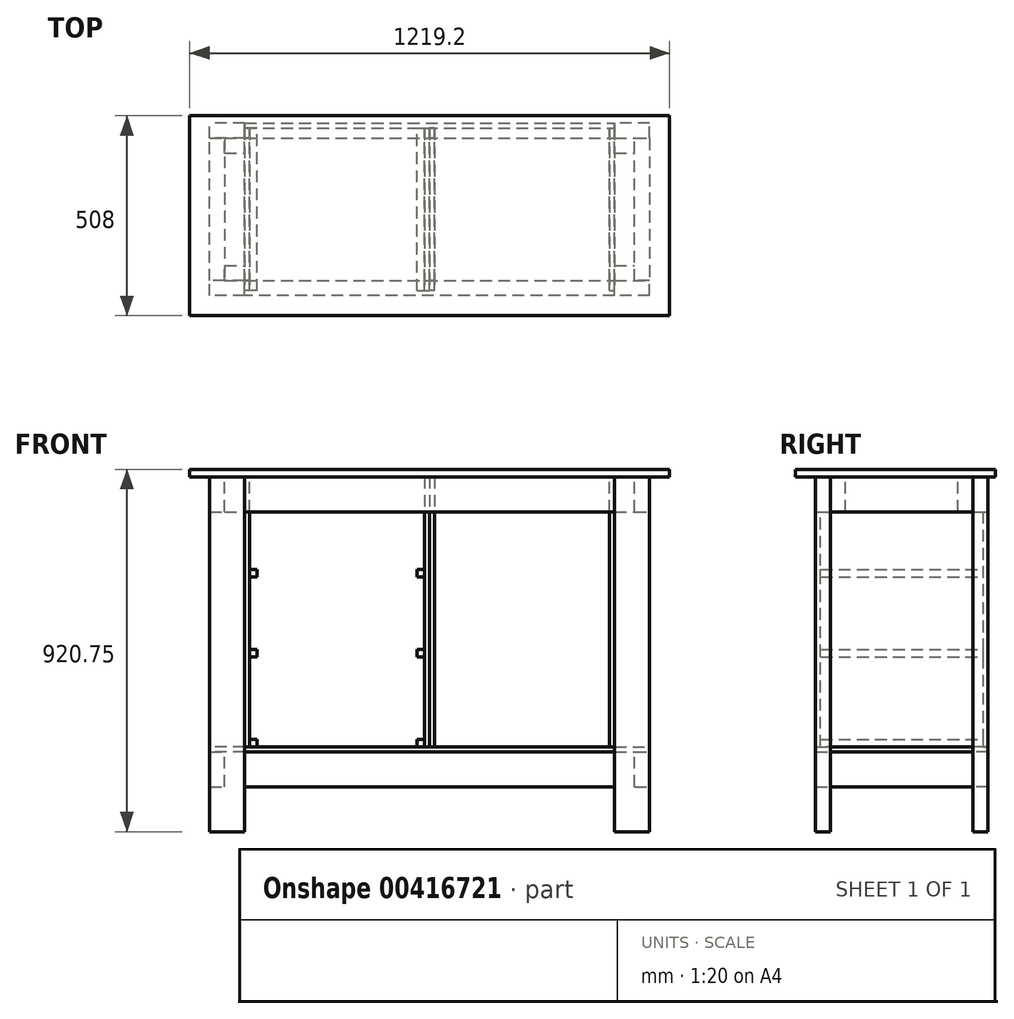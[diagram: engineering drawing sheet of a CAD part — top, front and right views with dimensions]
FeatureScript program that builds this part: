
annotation { "Feature Type Name" : "Feature", "Feature Type Description" : "" }
export const myFeature = defineFeature(function(context is Context, id is Id, definition is map)
    precondition{}
    {
        {
            var Q0;
            Q0=qCreatedBy(makeId("Front.planeOp"),FACE);
            var sketch = newSketch(context, id + "F0", { "sketchPlane" : qUnion([Q0])});
            skLineSegment(sketch, "E0.bottom", {"start": v(-609.6, 19.05) * mm, "end": v(609.6, 19.05) * mm});
            skLineSegment(sketch, "E0.top", {"start": v(-609.6, 0) * mm, "end": v(609.6, 0) * mm});
            skLineSegment(sketch, "E0.left", {"start": v(-609.6, 19.05) * mm, "end": v(-609.6, 0) * mm});
            skLineSegment(sketch, "E0.right", {"start": v(609.6, 19.05) * mm, "end": v(609.6, 0) * mm});
            skSolve(sketch);
        }
        {
            var Q0;
            Q0=qSketchRegion(id+"F0",true);
            extrude(context, id + "F1", {"entities" : qUnion([Q0]), "oppositeDirection" : true, "depth" : 508 * mm, "offsetDistance" : 25.4 * mm});
        }
        {
            var Q0;
            Q0=makeQuery(id+"F1.opExtrude","SWEPT_FACE",FACE,{"disambiguationData":[OSD([sQuery(id+"F0.wireOp",EDGE,"E0.top")])]});
            var sketch = newSketch(context, id + "F2", { "sketchPlane" : qUnion([Q0])});
            skLineSegment(sketch, "E1.0", {"start": v(558.8, -50.8) * mm, "end": v(-558.8, -50.8) * mm, "construction": true});
            skLineSegment(sketch, "E1.1", {"start": v(558.8, -488.95) * mm, "end": v(558.8, -50.8) * mm, "construction": true});
            skLineSegment(sketch, "E1.2", {"start": v(-558.8, -488.95) * mm, "end": v(558.8, -488.95) * mm, "construction": true});
            skLineSegment(sketch, "E1.3", {"start": v(-558.8, -50.8) * mm, "end": v(-558.8, -488.95) * mm, "construction": true});
            skSolve(sketch);
        }
        {
            var Q0;
            {var subQ0=sQuery(id+"F0.wireOp",EDGE,"E0.top");Q0=makeQuery(id+"F2.imprint","IMPRINT",FACE,{"disambiguationData":[TD([[makeQuery(id+"F2.imprint","IMPRINT",EDGE,{"derivedFrom":makeQuery(id+"F1.opExtrude","CAP_EDGE",EDGE,{"disambiguationData":[OSD([subQ0])],"isStart":true})}),-1.0]])]});}
            var sketch = newSketch(context, id + "F3", { "sketchPlane" : qUnion([Q0])});
            skLineSegment(sketch, "E2.bottom", {"start": v(558.8, -50.8) * mm, "end": v(469.9, -50.8) * mm});
            skLineSegment(sketch, "E2.top", {"start": v(558.8, -88.9) * mm, "end": v(469.9, -88.9) * mm});
            skLineSegment(sketch, "E2.left", {"start": v(558.8, -50.8) * mm, "end": v(558.8, -88.9) * mm});
            skLineSegment(sketch, "E2.right", {"start": v(469.9, -50.8) * mm, "end": v(469.9, -88.9) * mm});
            skLineSegment(sketch, "E3.bottom", {"start": v(-469.9, -50.8) * mm, "end": v(-558.8, -50.8) * mm});
            skLineSegment(sketch, "E3.top", {"start": v(-469.9, -88.9) * mm, "end": v(-558.8, -88.9) * mm});
            skLineSegment(sketch, "E3.left", {"start": v(-469.9, -50.8) * mm, "end": v(-469.9, -88.9) * mm});
            skLineSegment(sketch, "E3.right", {"start": v(-558.8, -50.8) * mm, "end": v(-558.8, -88.9) * mm});
            skLineSegment(sketch, "E4.bottom", {"start": v(-469.9, -450.85) * mm, "end": v(-558.8, -450.85) * mm});
            skLineSegment(sketch, "E4.top", {"start": v(-469.9, -488.95) * mm, "end": v(-558.8, -488.95) * mm});
            skLineSegment(sketch, "E4.left", {"start": v(-469.9, -450.85) * mm, "end": v(-469.9, -488.95) * mm});
            skLineSegment(sketch, "E4.right", {"start": v(-558.8, -450.85) * mm, "end": v(-558.8, -488.95) * mm});
            skLineSegment(sketch, "E5.bottom", {"start": v(558.8, -450.85) * mm, "end": v(469.9, -450.85) * mm});
            skLineSegment(sketch, "E5.top", {"start": v(558.8, -488.95) * mm, "end": v(469.9, -488.95) * mm});
            skLineSegment(sketch, "E5.left", {"start": v(558.8, -450.85) * mm, "end": v(558.8, -488.95) * mm});
            skLineSegment(sketch, "E5.right", {"start": v(469.9, -450.85) * mm, "end": v(469.9, -488.95) * mm});
            skSolve(sketch);
        }
        {
            var Q0;
            Q0=qSketchRegion(id+"F3",true);
            extrude(context, id + "F4", {"entities" : qUnion([Q0]), "depth" : 901.7 * mm, "offsetDistance" : 25.4 * mm});
        }
        {
            var Q0;
            {var subQ0=sQuery(id+"F0.wireOp",EDGE,"E0.top");Q0=makeQuery(id+"F2.imprint","IMPRINT",FACE,{"disambiguationData":[TD([[makeQuery(id+"F2.imprint","IMPRINT",EDGE,{"derivedFrom":makeQuery(id+"F1.opExtrude","CAP_EDGE",EDGE,{"disambiguationData":[OSD([subQ0])],"isStart":true})}),-1.0]])]});}
            var sketch = newSketch(context, id + "F5", { "sketchPlane" : qUnion([Q0])});
            skLineSegment(sketch, "E6.left", {"start": v(-558.8, -50.8) * mm, "end": v(-558.8, -50.8) * mm});
            skLineSegment(sketch, "E6.right", {"start": v(558.8, -50.8) * mm, "end": v(558.8, -50.8) * mm});
            skLineSegment(sketch, "E7.left", {"start": v(-558.8, -488.95) * mm, "end": v(-558.8, -488.95) * mm});
            skLineSegment(sketch, "E7.right", {"start": v(558.8, -488.95) * mm, "end": v(558.8, -488.95) * mm});
            skLineSegment(sketch, "E8.bottom", {"start": v(-469.9, -50.8) * mm, "end": v(469.9, -50.8) * mm});
            skLineSegment(sketch, "E8.top", {"start": v(-469.9, -88.9) * mm, "end": v(469.9, -88.9) * mm});
            skLineSegment(sketch, "E8.left", {"start": v(-469.9, -50.8) * mm, "end": v(-469.9, -88.9) * mm});
            skLineSegment(sketch, "E8.right", {"start": v(469.9, -50.8) * mm, "end": v(469.9, -88.9) * mm});
            skSolve(sketch);
        }
        {
            var Q0;
            Q0=makeQuery(id+"F5.imprint","IMPRINT",FACE,{"disambiguationData":[TD([[makeQuery(id+"F5.imprint","IMPRINT",EDGE,{"derivedFrom":sQuery(id+"F5.wireOp",EDGE,"E8.bottom")}),1.0]])]});
            var sketch = newSketch(context, id + "F6", { "sketchPlane" : qUnion([Q0])});
            skLineSegment(sketch, "E9.bottom", {"start": v(-469.9, -450.85) * mm, "end": v(469.9, -450.85) * mm});
            skLineSegment(sketch, "E9.top", {"start": v(-469.9, -488.95) * mm, "end": v(469.9, -488.95) * mm});
            skLineSegment(sketch, "E9.left", {"start": v(-469.9, -450.85) * mm, "end": v(-469.9, -488.95) * mm});
            skLineSegment(sketch, "E9.right", {"start": v(469.9, -450.85) * mm, "end": v(469.9, -488.95) * mm});
            skSolve(sketch);
        }
        {
            var Q0;
            Q0 = qSketchRegion(id + "F6", true);
            extrude(context, id + "F7", {"entities" : qUnion([Q0]), "depth" : 88.9 * mm, "offsetDistance" : 25.4 * mm});
        }
        {
            var Q0;
            Q0=qSketchRegion(id+"F5",true);
            extrude(context, id + "F8", {"entities" : qUnion([Q0]), "depth" : 88.9 * mm, "offsetDistance" : 25.4 * mm});
        }
        {
            var Q0;
            {var subQ0=sQuery(id+"F0.wireOp",EDGE,"E0.top");Q0=makeQuery(id+"F2.imprint","IMPRINT",FACE,{"disambiguationData":[TD([[makeQuery(id+"F2.imprint","IMPRINT",EDGE,{"derivedFrom":makeQuery(id+"F1.opExtrude","CAP_EDGE",EDGE,{"disambiguationData":[OSD([subQ0])],"isStart":true})}),-1.0]])]});}
            var sketch = newSketch(context, id + "F9", { "sketchPlane" : qUnion([Q0])});
            skLineSegment(sketch, "E10.bottom", {"start": v(-558.8, -88.9) * mm, "end": v(-520.7, -88.9) * mm});
            skLineSegment(sketch, "E10.top", {"start": v(-558.8, -450.85) * mm, "end": v(-520.7, -450.85) * mm});
            skLineSegment(sketch, "E10.left", {"start": v(-520.7, -88.9) * mm, "end": v(-520.7, -450.85) * mm});
            skLineSegment(sketch, "E10.right", {"start": v(-558.8, -88.9) * mm, "end": v(-558.8, -450.85) * mm});
            skLineSegment(sketch, "E11.bottom", {"start": v(520.7, -88.9) * mm, "end": v(558.8, -88.9) * mm});
            skLineSegment(sketch, "E11.top", {"start": v(520.7, -450.85) * mm, "end": v(558.8, -450.85) * mm});
            skLineSegment(sketch, "E11.left", {"start": v(558.8, -88.9) * mm, "end": v(558.8, -450.85) * mm});
            skLineSegment(sketch, "E11.right", {"start": v(520.7, -88.9) * mm, "end": v(520.7, -450.85) * mm});
            skSolve(sketch);
        }
        {
            var Q0;
            Q0=qSketchRegion(id+"F9",true);
            extrude(context, id + "F10", {"entities" : qUnion([Q0]), "depth" : 88.9 * mm, "offsetDistance" : 25.4 * mm});
        }
        {
            var Q0;
            Q0=makeQuery(id+"F1.opExtrude","SWEPT_FACE",FACE,{"disambiguationData":[OSD([sQuery(id+"F0.wireOp",EDGE,"E0.top")])]});
            var sketch = newSketch(context, id + "F11", { "sketchPlane" : qUnion([Q0])});
            skLineSegment(sketch, "E12.bottom", {"start": v(-520.7, -88.9) * mm, "end": v(-469.9, -88.9) * mm});
            skLineSegment(sketch, "E12.top", {"start": v(-520.7, -127) * mm, "end": v(-469.9, -127) * mm});
            skLineSegment(sketch, "E12.left", {"start": v(-520.7, -88.9) * mm, "end": v(-520.7, -127) * mm});
            skLineSegment(sketch, "E12.right", {"start": v(-469.9, -88.9) * mm, "end": v(-469.9, -127) * mm});
            skLineSegment(sketch, "E13.bottom", {"start": v(-520.7, -412.75) * mm, "end": v(-469.9, -412.75) * mm});
            skLineSegment(sketch, "E13.top", {"start": v(-520.7, -450.85) * mm, "end": v(-469.9, -450.85) * mm});
            skLineSegment(sketch, "E13.left", {"start": v(-520.7, -412.75) * mm, "end": v(-520.7, -450.85) * mm});
            skLineSegment(sketch, "E13.right", {"start": v(-469.9, -412.75) * mm, "end": v(-469.9, -450.85) * mm});
            skLineSegment(sketch, "E14.bottom", {"start": v(469.9, -88.9) * mm, "end": v(520.7, -88.9) * mm});
            skLineSegment(sketch, "E14.top", {"start": v(469.9, -127) * mm, "end": v(520.7, -127) * mm});
            skLineSegment(sketch, "E14.left", {"start": v(469.9, -88.9) * mm, "end": v(469.9, -127) * mm});
            skLineSegment(sketch, "E14.right", {"start": v(520.7, -88.9) * mm, "end": v(520.7, -127) * mm});
            skLineSegment(sketch, "E15.bottom", {"start": v(469.9, -412.75) * mm, "end": v(520.7, -412.75) * mm});
            skLineSegment(sketch, "E15.top", {"start": v(469.9, -450.85) * mm, "end": v(520.7, -450.85) * mm});
            skLineSegment(sketch, "E15.left", {"start": v(469.9, -412.75) * mm, "end": v(469.9, -450.85) * mm});
            skLineSegment(sketch, "E15.right", {"start": v(520.7, -412.75) * mm, "end": v(520.7, -450.85) * mm});
            skSolve(sketch);
        }
        {
            var Q0;
            Q0 = qSketchRegion(id + "F11", true);
            extrude(context, id + "F12", {"entities" : qUnion([Q0]), "depth" : 88.9 * mm, "offsetDistance" : 25.4 * mm});
        }
        {
            var Q0;
            Q0=makeQuery(id+"F4.opExtrude","CAP_FACE",FACE,{"disambiguationData":[OSD([sQuery(id+"F3.wireOp",EDGE,"E3.bottom"),sQuery(id+"F3.wireOp",EDGE,"E3.top"),sQuery(id+"F3.wireOp",EDGE,"E3.left"),sQuery(id+"F3.wireOp",EDGE,"E3.right")])],"isStart":false});
            cPlane(context, id + "F13", {"entities" : qUnion([Q0]), "cplaneType" : CPlaneType.OFFSET, "offset" : 203.2 * mm, "oppositeDirection" : true, "width" : 152.4 * mm, "height" : 152.4 * mm});
        }
        {
            var Q0;
            Q0=qCreatedBy(id+"F13.planeOp",FACE);
            var sketch = newSketch(context, id + "F14", { "sketchPlane" : qUnion([Q0])});
            skLineSegment(sketch, "E16.0.0", {"start": v(-469.9, -50.8) * mm, "end": v(-469.9, -88.9) * mm});
            skLineSegment(sketch, "E16.0.1", {"start": v(-469.9, -88.9) * mm, "end": v(469.9, -88.9) * mm});
            skLineSegment(sketch, "E16.0.2", {"start": v(469.9, -88.9) * mm, "end": v(469.9, -50.8) * mm});
            skLineSegment(sketch, "E16.0.3", {"start": v(469.9, -50.8) * mm, "end": v(-469.9, -50.8) * mm});
            skLineSegment(sketch, "E17.0.0", {"start": v(-469.9, -488.95) * mm, "end": v(-469.9, -450.85) * mm});
            skLineSegment(sketch, "E17.0.1", {"start": v(-469.9, -450.85) * mm, "end": v(469.9, -450.85) * mm});
            skLineSegment(sketch, "E17.0.2", {"start": v(469.9, -488.95) * mm, "end": v(469.9, -450.85) * mm});
            skLineSegment(sketch, "E17.0.3", {"start": v(469.9, -488.95) * mm, "end": v(-469.9, -488.95) * mm});
            skSolve(sketch);
        }
        {
            var Q0;
            Q0=qSketchRegion(id+"F14",true);
            extrude(context, id + "F15", {"entities" : qUnion([Q0]), "depth" : 88.9 * mm, "offsetDistance" : 25.4 * mm});
        }
        {
            var Q0;
            Q0=qCreatedBy(id+"F13.planeOp",FACE);
            var sketch = newSketch(context, id + "F16", { "sketchPlane" : qUnion([Q0])});
            skLineSegment(sketch, "E18.0.0", {"start": v(-520.7, -450.85) * mm, "end": v(-520.7, -88.9) * mm});
            skLineSegment(sketch, "E18.0.1", {"start": v(-558.8, -450.85) * mm, "end": v(-520.7, -450.85) * mm});
            skLineSegment(sketch, "E18.0.2", {"start": v(-558.8, -88.9) * mm, "end": v(-558.8, -450.85) * mm});
            skLineSegment(sketch, "E18.0.3", {"start": v(-520.7, -88.9) * mm, "end": v(-558.8, -88.9) * mm});
            skLineSegment(sketch, "E19.0.0", {"start": v(558.8, -450.85) * mm, "end": v(558.8, -88.9) * mm});
            skLineSegment(sketch, "E19.0.1", {"start": v(520.7, -450.85) * mm, "end": v(558.8, -450.85) * mm});
            skLineSegment(sketch, "E19.0.2", {"start": v(520.7, -88.9) * mm, "end": v(520.7, -450.85) * mm});
            skLineSegment(sketch, "E19.0.3", {"start": v(558.8, -88.9) * mm, "end": v(520.7, -88.9) * mm});
            skSolve(sketch);
        }
        {
            var Q0;
            Q0=qSketchRegion(id+"F16",true);
            extrude(context, id + "F17", {"entities" : qUnion([Q0]), "depth" : 88.9 * mm, "offsetDistance" : 25.4 * mm});
        }
        {
            var Q0;
            Q0=qCreatedBy(id+"F13.planeOp",FACE);
            var sketch = newSketch(context, id + "F18", { "sketchPlane" : qUnion([Q0])});
            skLineSegment(sketch, "E20", {"start": v(558.8, -450.85) * mm, "end": v(558.8, -88.9) * mm});
            skLineSegment(sketch, "E21", {"start": v(469.9, -50.8) * mm, "end": v(-469.9, -50.8) * mm});
            skLineSegment(sketch, "E22", {"start": v(-558.8, -88.9) * mm, "end": v(-558.8, -450.85) * mm});
            skLineSegment(sketch, "E23", {"start": v(-469.9, -488.95) * mm, "end": v(469.9, -488.95) * mm});
            skLineSegment(sketch, "E24", {"start": v(-469.9, -50.8) * mm, "end": v(-469.9, -88.9) * mm});
            skLineSegment(sketch, "E25", {"start": v(-469.9, -88.9) * mm, "end": v(-558.8, -88.9) * mm});
            skLineSegment(sketch, "E26", {"start": v(-469.9, -488.95) * mm, "end": v(-469.9, -450.85) * mm});
            skLineSegment(sketch, "E27", {"start": v(-469.9, -450.85) * mm, "end": v(-558.8, -450.85) * mm});
            skLineSegment(sketch, "E28", {"start": v(469.9, -488.95) * mm, "end": v(469.9, -450.85) * mm});
            skLineSegment(sketch, "E29", {"start": v(469.9, -450.85) * mm, "end": v(558.8, -450.85) * mm});
            skLineSegment(sketch, "E30", {"start": v(469.9, -50.8) * mm, "end": v(469.9, -88.9) * mm});
            skLineSegment(sketch, "E31", {"start": v(469.9, -88.9) * mm, "end": v(558.8, -88.9) * mm});
            skSolve(sketch);
        }
        {
            var Q0;
            Q0=qSketchRegion(id+"F18",true);
            extrude(context, id + "F19", {"entities" : qUnion([Q0]), "oppositeDirection" : true, "depth" : 12.7 * mm, "offsetDistance" : 25.4 * mm});
        }
        {
            var Q0;
            Q0=qCreatedBy(makeId("Right.planeOp"),FACE);
            var sketch = newSketch(context, id + "F20", { "sketchPlane" : qUnion([Q0])});
            skLineSegment(sketch, "E32", {"start": v(450.85, 0) * mm, "end": v(450.85, -88.9) * mm});
            skLineSegment(sketch, "E33", {"start": v(450.85, -88.9) * mm, "end": v(476.25, -88.9) * mm});
            skLineSegment(sketch, "E34", {"start": v(476.25, -88.9) * mm, "end": v(476.25, -685.8) * mm});
            skLineSegment(sketch, "E35", {"start": v(476.25, -685.8) * mm, "end": v(63.5, -685.8) * mm});
            skLineSegment(sketch, "E36", {"start": v(63.5, -685.8) * mm, "end": v(63.5, -88.9) * mm});
            skLineSegment(sketch, "E37", {"start": v(63.5, -88.9) * mm, "end": v(88.9, -88.9) * mm});
            skLineSegment(sketch, "E38", {"start": v(88.9, -88.9) * mm, "end": v(88.9, 0) * mm});
            skLineSegment(sketch, "E39", {"start": v(88.9, 0) * mm, "end": v(450.85, 0) * mm});
            skSolve(sketch);
        }
        {
            var Q0;
            Q0 = qSketchRegion(id + "F20", true);
            extrude(context, id + "F21", {"entities" : qUnion([Q0]), "depth" : 12.7 * mm, "offsetDistance" : 25.4 * mm});
        }
        {
            var Q0;
            Q0 = qSketchRegion(id + "F20", true);
            extrude(context, id + "F22", {"entities" : qUnion([Q0]), "oppositeDirection" : true, "depth" : 12.7 * mm, "offsetDistance" : 25.4 * mm});
        }
        {
            var Q0;
            Q0=makeQuery(id+"F12.opExtrude","SWEPT_FACE",FACE,{"disambiguationData":[OSD([sQuery(id+"F11.wireOp",EDGE,"E13.right")])]});
            var sketch = newSketch(context, id + "F23", { "sketchPlane" : qUnion([Q0])});
            skLineSegment(sketch, "E40.0", {"start": v(450.85, 0) * mm, "end": v(450.85, -88.9) * mm});
            skLineSegment(sketch, "E40.1", {"start": v(450.85, -88.9) * mm, "end": v(476.25, -88.9) * mm});
            skLineSegment(sketch, "E40.2", {"start": v(476.25, -88.9) * mm, "end": v(476.25, -685.8) * mm});
            skLineSegment(sketch, "E40.3", {"start": v(476.25, -685.8) * mm, "end": v(63.5, -685.8) * mm});
            skLineSegment(sketch, "E40.4", {"start": v(63.5, -685.8) * mm, "end": v(63.5, -88.9) * mm});
            skLineSegment(sketch, "E40.5", {"start": v(63.5, -88.9) * mm, "end": v(88.9, -88.9) * mm});
            skLineSegment(sketch, "E40.6", {"start": v(88.9, -88.9) * mm, "end": v(88.9, 0) * mm});
            skLineSegment(sketch, "E40.7", {"start": v(88.9, 0) * mm, "end": v(450.85, 0) * mm});
            skSolve(sketch);
        }
        {
            var Q0;
            Q0 = qSketchRegion(id + "F23", true);
            extrude(context, id + "F24", {"entities" : qUnion([Q0]), "depth" : 12.7 * mm, "offsetDistance" : 25.4 * mm});
        }
        {
            var Q0;
            Q0=makeQuery(id+"F12.opExtrude","SWEPT_FACE",FACE,{"disambiguationData":[OSD([sQuery(id+"F11.wireOp",EDGE,"E15.left")])]});
            var sketch = newSketch(context, id + "F25", { "sketchPlane" : qUnion([Q0])});
            skLineSegment(sketch, "E41.0", {"start": v(-450.85, 0) * mm, "end": v(-450.85, -88.9) * mm});
            skLineSegment(sketch, "E41.1", {"start": v(-450.85, -88.9) * mm, "end": v(-476.25, -88.9) * mm});
            skLineSegment(sketch, "E41.2", {"start": v(-476.25, -88.9) * mm, "end": v(-476.25, -685.8) * mm});
            skLineSegment(sketch, "E41.3", {"start": v(-476.25, -685.8) * mm, "end": v(-63.5, -685.8) * mm});
            skLineSegment(sketch, "E41.4", {"start": v(-63.5, -685.8) * mm, "end": v(-63.5, -88.9) * mm});
            skLineSegment(sketch, "E41.5", {"start": v(-63.5, -88.9) * mm, "end": v(-88.9, -88.9) * mm});
            skLineSegment(sketch, "E41.6", {"start": v(-88.9, -88.9) * mm, "end": v(-88.9, 0) * mm});
            skLineSegment(sketch, "E41.7", {"start": v(-88.9, 0) * mm, "end": v(-450.85, 0) * mm});
            skSolve(sketch);
        }
        {
            var Q0;
            Q0 = qSketchRegion(id + "F25", true);
            extrude(context, id + "F26", {"entities" : qUnion([Q0]), "depth" : 12.7 * mm, "offsetDistance" : 25.4 * mm});
        }
        {
            var Q0;
            Q0=makeQuery(id+"F7.opExtrude","CAP_FACE",FACE,{"disambiguationData":[OSD([sQuery(id+"F6.wireOp",EDGE,"E9.bottom"),sQuery(id+"F6.wireOp",EDGE,"E9.top"),sQuery(id+"F6.wireOp",EDGE,"E9.left"),sQuery(id+"F6.wireOp",EDGE,"E9.right")])],"isStart":false});
            var sketch = newSketch(context, id + "F27", { "sketchPlane" : qUnion([Q0])});
            skLineSegment(sketch, "E42.bottom", {"start": v(-469.9, -488.95) * mm, "end": v(469.9, -488.95) * mm});
            skLineSegment(sketch, "E42.top", {"start": v(-469.9, -476.25) * mm, "end": v(469.9, -476.25) * mm});
            skLineSegment(sketch, "E42.left", {"start": v(-469.9, -488.95) * mm, "end": v(-469.9, -476.25) * mm});
            skLineSegment(sketch, "E42.right", {"start": v(469.9, -488.95) * mm, "end": v(469.9, -476.25) * mm});
            skSolve(sketch);
        }
        {
            var Q0;
            Q0 = qSketchRegion(id + "F27", true);
            extrude(context, id + "F28", {"entities" : qUnion([Q0]), "depth" : 596.9 * mm, "offsetDistance" : 25.4 * mm});
        }
        {
            var Q0;
            Q0=makeQuery(id+"F21.opExtrude","SWEPT_FACE",FACE,{"disambiguationData":[OSD([sQuery(id+"F20.wireOp",EDGE,"E36")])]});
            var sketch = newSketch(context, id + "F29", { "sketchPlane" : qUnion([Q0])});
            skLineSegment(sketch, "E43.bottom", {"start": v(-457.2, -107.95) * mm, "end": v(-12.7, -107.95) * mm});
            skLineSegment(sketch, "E43.top", {"start": v(-457.2, -234.95) * mm, "end": v(-12.7, -234.95) * mm});
            skLineSegment(sketch, "E43.left", {"start": v(-457.2, -107.95) * mm, "end": v(-457.2, -234.95) * mm});
            skLineSegment(sketch, "E43.right", {"start": v(-12.7, -107.95) * mm, "end": v(-12.7, -234.95) * mm});
            skLineSegment(sketch, "E44.bottom", {"start": v(-457.2, -254) * mm, "end": v(-12.7, -254) * mm});
            skLineSegment(sketch, "E44.top", {"start": v(-457.2, -438.15) * mm, "end": v(-12.7, -438.15) * mm});
            skLineSegment(sketch, "E44.left", {"start": v(-457.2, -254) * mm, "end": v(-457.2, -438.15) * mm});
            skLineSegment(sketch, "E44.right", {"start": v(-12.7, -254) * mm, "end": v(-12.7, -438.15) * mm});
            skLineSegment(sketch, "E45.bottom", {"start": v(-457.2, -457.2) * mm, "end": v(-12.7, -457.2) * mm});
            skLineSegment(sketch, "E45.top", {"start": v(-457.2, -666.75) * mm, "end": v(-12.7, -666.75) * mm});
            skLineSegment(sketch, "E45.left", {"start": v(-457.2, -457.2) * mm, "end": v(-457.2, -666.75) * mm});
            skLineSegment(sketch, "E45.right", {"start": v(-12.7, -457.2) * mm, "end": v(-12.7, -666.75) * mm});
            skSolve(sketch);
        }
        {
            var Q0;
            Q0=makeQuery(id+"F24.opExtrude","CAP_FACE",FACE,{"disambiguationData":[OSD([sQuery(id+"F23.wireOp",EDGE,"E40.0"),sQuery(id+"F23.wireOp",EDGE,"E40.1"),sQuery(id+"F23.wireOp",EDGE,"E40.2"),sQuery(id+"F23.wireOp",EDGE,"E40.3"),sQuery(id+"F23.wireOp",EDGE,"E40.4"),sQuery(id+"F23.wireOp",EDGE,"E40.5"),sQuery(id+"F23.wireOp",EDGE,"E40.6"),sQuery(id+"F23.wireOp",EDGE,"E40.7")])],"isStart":false});
            var sketch = newSketch(context, id + "F30", { "sketchPlane" : qUnion([Q0])});
            skLineSegment(sketch, "E46.bottom", {"start": v(63.5, -234.95) * mm, "end": v(476.25, -234.95) * mm});
            skLineSegment(sketch, "E46.top", {"start": v(63.5, -254) * mm, "end": v(476.25, -254) * mm});
            skLineSegment(sketch, "E46.left", {"start": v(63.5, -234.95) * mm, "end": v(63.5, -254) * mm});
            skLineSegment(sketch, "E46.right", {"start": v(476.25, -234.95) * mm, "end": v(476.25, -254) * mm});
            skLineSegment(sketch, "E47.bottom", {"start": v(63.5, -438.15) * mm, "end": v(476.25, -438.15) * mm});
            skLineSegment(sketch, "E47.top", {"start": v(63.5, -457.2) * mm, "end": v(476.25, -457.2) * mm});
            skLineSegment(sketch, "E47.left", {"start": v(63.5, -438.15) * mm, "end": v(63.5, -457.2) * mm});
            skLineSegment(sketch, "E47.right", {"start": v(476.25, -438.15) * mm, "end": v(476.25, -457.2) * mm});
            skLineSegment(sketch, "E48.bottom", {"start": v(63.5, -666.75) * mm, "end": v(476.25, -666.75) * mm});
            skLineSegment(sketch, "E48.top", {"start": v(63.5, -685.8) * mm, "end": v(476.25, -685.8) * mm});
            skLineSegment(sketch, "E48.left", {"start": v(63.5, -666.75) * mm, "end": v(63.5, -685.8) * mm});
            skLineSegment(sketch, "E48.right", {"start": v(476.25, -666.75) * mm, "end": v(476.25, -685.8) * mm});
            skSolve(sketch);
        }
        {
            var Q0;
            Q0 = qSketchRegion(id + "F30", true);
            extrude(context, id + "F31", {"entities" : qUnion([Q0]), "depth" : 19.05 * mm, "offsetDistance" : 25.4 * mm});
        }
        {
            var Q0;
            Q0=makeQuery(id+"F22.opExtrude","CAP_FACE",FACE,{"disambiguationData":[OSD([sQuery(id+"F20.wireOp",EDGE,"E32"),sQuery(id+"F20.wireOp",EDGE,"E33"),sQuery(id+"F20.wireOp",EDGE,"E34"),sQuery(id+"F20.wireOp",EDGE,"E35"),sQuery(id+"F20.wireOp",EDGE,"E36"),sQuery(id+"F20.wireOp",EDGE,"E37"),sQuery(id+"F20.wireOp",EDGE,"E38"),sQuery(id+"F20.wireOp",EDGE,"E39")])],"isStart":false});
            var sketch = newSketch(context, id + "F32", { "sketchPlane" : qUnion([Q0])});
            skLineSegment(sketch, "E49.0", {"start": v(-63.5, -234.95) * mm, "end": v(-476.25, -234.95) * mm});
            skLineSegment(sketch, "E49.1", {"start": v(-63.5, -254) * mm, "end": v(-476.25, -254) * mm});
            skLineSegment(sketch, "E49.2", {"start": v(-63.5, -234.95) * mm, "end": v(-63.5, -254) * mm});
            skLineSegment(sketch, "E49.3", {"start": v(-476.25, -234.95) * mm, "end": v(-476.25, -254) * mm});
            skLineSegment(sketch, "E49.8", {"start": v(-63.5, -438.15) * mm, "end": v(-476.25, -438.15) * mm});
            skLineSegment(sketch, "E49.9", {"start": v(-63.5, -457.2) * mm, "end": v(-476.25, -457.2) * mm});
            skLineSegment(sketch, "E49.10", {"start": v(-63.5, -438.15) * mm, "end": v(-63.5, -457.2) * mm});
            skLineSegment(sketch, "E49.11", {"start": v(-476.25, -438.15) * mm, "end": v(-476.25, -457.2) * mm});
            skLineSegment(sketch, "E49.12", {"start": v(-63.5, -666.75) * mm, "end": v(-476.25, -666.75) * mm});
            skLineSegment(sketch, "E49.13", {"start": v(-63.5, -685.8) * mm, "end": v(-476.25, -685.8) * mm});
            skLineSegment(sketch, "E49.14", {"start": v(-63.5, -666.75) * mm, "end": v(-63.5, -685.8) * mm});
            skLineSegment(sketch, "E49.15", {"start": v(-476.25, -666.75) * mm, "end": v(-476.25, -685.8) * mm});
            skPoint(sketch, "E49.6.end.orphan", {"position": v(-63.5, -107.95) * mm});
            skPoint(sketch, "E49.6.start.orphan", {"position": v(-63.5, -88.9) * mm});
            skPoint(sketch, "E49.4.end.orphan", {"position": v(-476.25, -88.9) * mm});
            skPoint(sketch, "E49.4.start.orphan", {"position": v(-63.5, -88.9) * mm});
            skPoint(sketch, "E49.5.end.orphan", {"position": v(-476.25, -107.95) * mm});
            skPoint(sketch, "E49.5.start.orphan", {"position": v(-63.5, -107.95) * mm});
            skPoint(sketch, "E49.7.end.orphan", {"position": v(-476.25, -107.95) * mm});
            skPoint(sketch, "E49.7.start.orphan", {"position": v(-476.25, -88.9) * mm});
            skSolve(sketch);
        }
        {
            var Q0;
            Q0 = qSketchRegion(id + "F32", true);
            extrude(context, id + "F33", {"entities" : qUnion([Q0]), "depth" : 19.05 * mm, "offsetDistance" : 25.4 * mm});
        }
    });
